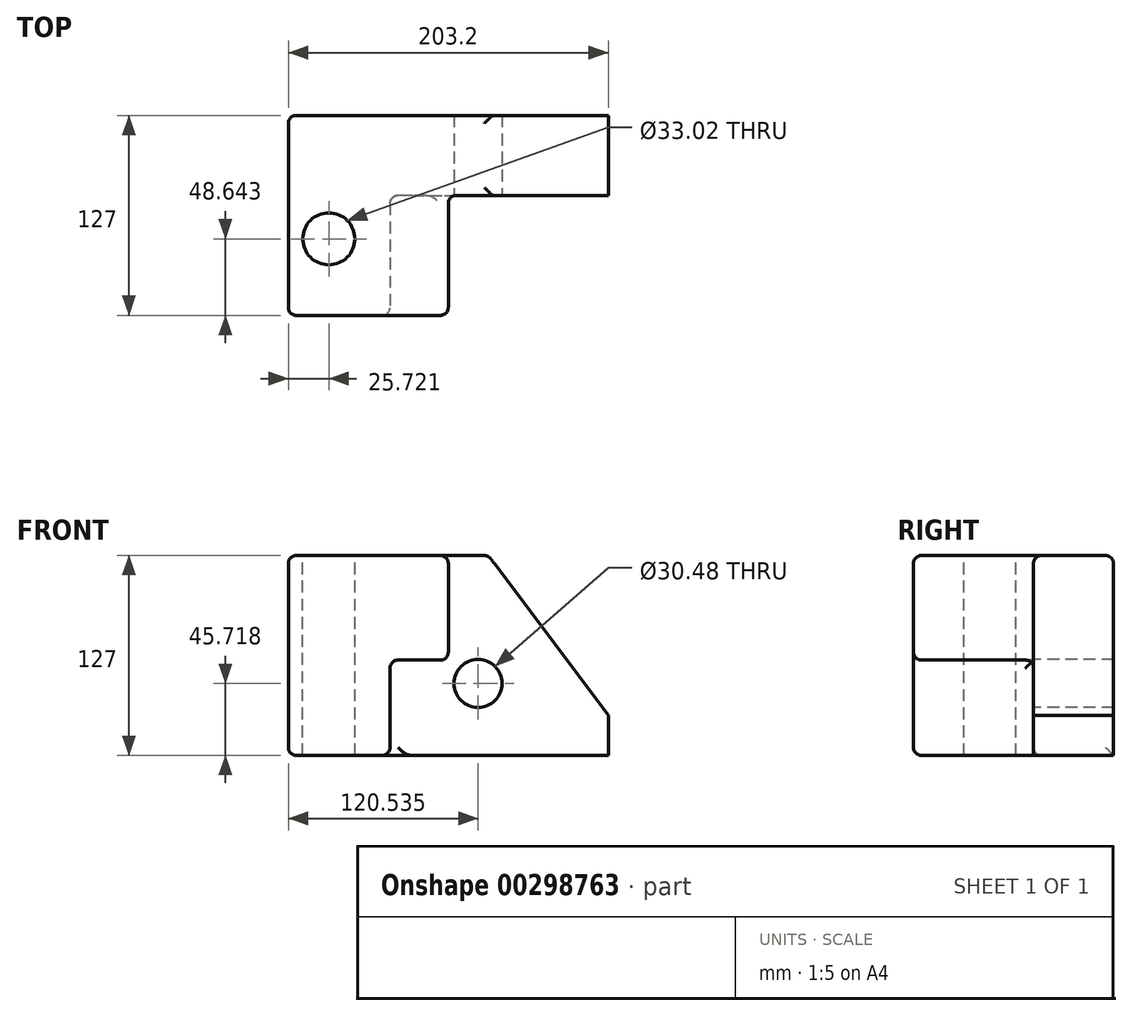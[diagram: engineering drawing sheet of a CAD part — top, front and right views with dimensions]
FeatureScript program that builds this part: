
annotation { "Feature Type Name" : "Feature", "Feature Type Description" : "" }
export const myFeature = defineFeature(function(context is Context, id is Id, definition is map)
    precondition{}
    {
        {
            var Q0;
            Q0=qCreatedBy(makeId("Front.planeOp"),FACE);
            var sketch = newSketch(context, id + "F0", { "sketchPlane" : qUnion([Q0])});
            skLineSegment(sketch, "E0.bottom", {"start": v(-101.6, 66.42) * mm, "end": v(101.6, 66.42) * mm});
            skLineSegment(sketch, "E0.top", {"start": v(-101.6, -60.58) * mm, "end": v(101.6, -60.58) * mm});
            skLineSegment(sketch, "E0.left", {"start": v(-101.6, 66.42) * mm, "end": v(-101.6, -60.58) * mm});
            skLineSegment(sketch, "E0.right", {"start": v(101.6, 66.42) * mm, "end": v(101.6, -60.58) * mm});
            skPoint(sketch, "E0.middle", {"position": v(0, 2.92) * mm});
            skSolve(sketch);
        }
        {
            var Q0;
            Q0=makeQuery(id+"F0.imprint","IMPRINT",FACE,{"disambiguationData":[TD([[makeQuery(id+"F0.imprint","IMPRINT",EDGE,{"derivedFrom":sQuery(id+"F0.wireOp",EDGE,"E0.bottom")}),-1.0]])]});
            extrude(context, id + "F1", {"entities" : qUnion([Q0]), "depth" : 127 * mm});
        }
        {
            var Q0;
            Q0=makeQuery(id+"F1.opExtrude","CAP_FACE",FACE,{"disambiguationData":[OSD([sQuery(id+"F0.wireOp",EDGE,"E0.bottom"),sQuery(id+"F0.wireOp",EDGE,"E0.top"),sQuery(id+"F0.wireOp",EDGE,"E0.left"),sQuery(id+"F0.wireOp",EDGE,"E0.right")])],"isStart":false});
            var sketch = newSketch(context, id + "F2", { "sketchPlane" : qUnion([Q0])});
            skLineSegment(sketch, "E1", {"start": v(-101.6, -60.58) * mm, "end": v(-101.6, 66.42) * mm});
            skLineSegment(sketch, "E2", {"start": v(-101.6, 66.42) * mm, "end": v(0, 66.42) * mm});
            skLineSegment(sketch, "E3", {"start": v(0, 66.42) * mm, "end": v(0, 0) * mm});
            skLineSegment(sketch, "E4", {"start": v(0, 0) * mm, "end": v(-36.95, 0) * mm});
            skLineSegment(sketch, "E5", {"start": v(-36.95, 0) * mm, "end": v(-36.95, -60.58) * mm});
            skLineSegment(sketch, "E6", {"start": v(-36.95, -60.58) * mm, "end": v(-101.6, -60.58) * mm});
            skSolve(sketch);
        }
        {
            var Q0;
            {var subQ2=sQuery(id+"F2.wireOp",EDGE,"E3");Q0=makeQuery(id+"F2.imprint","IMPRINT",FACE,{"disambiguationData":[TD([[makeQuery(id+"F2.imprint","IMPRINT",EDGE,{"derivedFrom":subQ2}),1.0]])]});}
            extrude(context, id + "F3", {"entities" : qUnion([Q0]), "operationType" : NewBodyOperationType.REMOVE, "oppositeDirection" : true, "depth" : 76.2 * mm});
        }
        {
            var Q0;
            Q0=makeQuery(id+"F1.opExtrude","SWEPT_EDGE",EDGE,{"disambiguationData":[OSD([sQuery(id+"F0.wireOp",EDGE,"E0.bottom"),sQuery(id+"F0.wireOp",EDGE,"E0.right")])]});
            chamfer(context, id + "F4", {"entities" : qUnion([Q0]), "chamferType" : ChamferType.TWO_OFFSETS, "width1" : 76.2 * mm, "oppositeDirection" : false, "width2" : 101.6 * mm, "tangentPropagation" : true});
        }
        {
            var Q0;
            Q0=makeQuery(id+"F1.opExtrude","SWEPT_FACE",FACE,{"disambiguationData":[OSD([sQuery(id+"F0.wireOp",EDGE,"E0.bottom")])]});
            var Q1;
            Q1=makeQuery(id+"F3.boolean.opBoolean","COPY",FACE,{"derivedFrom":makeQuery(id+"F3.opExtrude","SWEPT_FACE",FACE,{"disambiguationData":[OSD([sQuery(id+"F2.wireOp",EDGE,"E3")])]})});
            var Q2;
            Q2=makeQuery(id+"F1.opExtrude","CAP_FACE",FACE,{"disambiguationData":[OSD([sQuery(id+"F0.wireOp",EDGE,"E0.bottom"),sQuery(id+"F0.wireOp",EDGE,"E0.top"),sQuery(id+"F0.wireOp",EDGE,"E0.left"),sQuery(id+"F0.wireOp",EDGE,"E0.right")])],"isStart":false});
            var Q3;
            Q3=makeQuery(id+"F3.boolean.opBoolean","COPY",FACE,{"derivedFrom":makeQuery(id+"F3.opExtrude","SWEPT_FACE",FACE,{"disambiguationData":[OSD([sQuery(id+"F2.wireOp",EDGE,"E5")])]})});
            var Q4;
            Q4=makeQuery(id+"F1.opExtrude","SWEPT_FACE",FACE,{"disambiguationData":[OSD([sQuery(id+"F0.wireOp",EDGE,"E0.left")])]});
            fillet(context, id + "F5", {"entities" : qUnion([Q0, Q1, Q2, Q3, Q4]), "radius" : 5.08 * mm, "tangentPropagation" : true, "allowEdgeOverflow" : false});
        }
        {
            var Q0;
            Q0=makeQuery(id+"F3.boolean.opBoolean","COPY",FACE,{"derivedFrom":makeQuery(id+"F3.opExtrude","CAP_FACE",FACE,{"disambiguationData":[OSD([sQuery(id+"F0.wireOp",EDGE,"E0.bottom"),sQuery(id+"F0.wireOp",EDGE,"E0.top"),sQuery(id+"F0.wireOp",EDGE,"E0.right"),sQuery(id+"F2.wireOp",EDGE,"E3"),sQuery(id+"F2.wireOp",EDGE,"E4"),sQuery(id+"F2.wireOp",EDGE,"E5")])],"isStart":false})});
            var sketch = newSketch(context, id + "F6", { "sketchPlane" : qUnion([Q0])});
            skCircle(sketch, "E7", {"center": v(18.93, -14.86) * mm, "radius": 15.24 * mm});
            skSolve(sketch);
        }
        {
            var Q0;
            Q0=makeQuery(id+"F6.imprint","IMPRINT",FACE,{"disambiguationData":[TD([[makeQuery(id+"F6.imprint","IMPRINT",EDGE,{"derivedFrom":sQuery(id+"F6.wireOp",EDGE,"E7")}),1.0]])]});
            var Q1;
            Q1=makeQuery(id+"F1.opExtrude","CAP_FACE",FACE,{"disambiguationData":[OSD([sQuery(id+"F0.wireOp",EDGE,"E0.bottom"),sQuery(id+"F0.wireOp",EDGE,"E0.top"),sQuery(id+"F0.wireOp",EDGE,"E0.left"),sQuery(id+"F0.wireOp",EDGE,"E0.right")])],"isStart":true});
            extrude(context, id + "F7", {"entities" : qUnion([Q0]), "operationType" : NewBodyOperationType.REMOVE, "endBound" : BoundingType.UP_TO_SURFACE, "oppositeDirection" : true, "endBoundEntityFace" : qUnion([Q1]), "depth" : 25.4 * mm});
        }
        {
            var Q0;
            Q0=makeQuery(id+"F1.opExtrude","SWEPT_FACE",FACE,{"disambiguationData":[OSD([sQuery(id+"F0.wireOp",EDGE,"E0.bottom")])]});
            var sketch = newSketch(context, id + "F8", { "sketchPlane" : qUnion([Q0])});
            skCircle(sketch, "E8", {"center": v(-75.88, -78.36) * mm, "radius": 16.51 * mm});
            skSolve(sketch);
        }
        {
            var Q0;
            Q0=makeQuery(id+"F8.imprint","IMPRINT",FACE,{"disambiguationData":[TD([[makeQuery(id+"F8.imprint","IMPRINT",EDGE,{"derivedFrom":sQuery(id+"F8.wireOp",EDGE,"E8")}),1.0]])]});
            var Q1;
            Q1=makeQuery(id+"F1.opExtrude","SWEPT_FACE",FACE,{"disambiguationData":[OSD([sQuery(id+"F0.wireOp",EDGE,"E0.top")])]});
            extrude(context, id + "F9", {"entities" : qUnion([Q0]), "operationType" : NewBodyOperationType.REMOVE, "endBound" : BoundingType.UP_TO_SURFACE, "oppositeDirection" : true, "endBoundEntityFace" : qUnion([Q1]), "depth" : 25.4 * mm});
        }
    });
